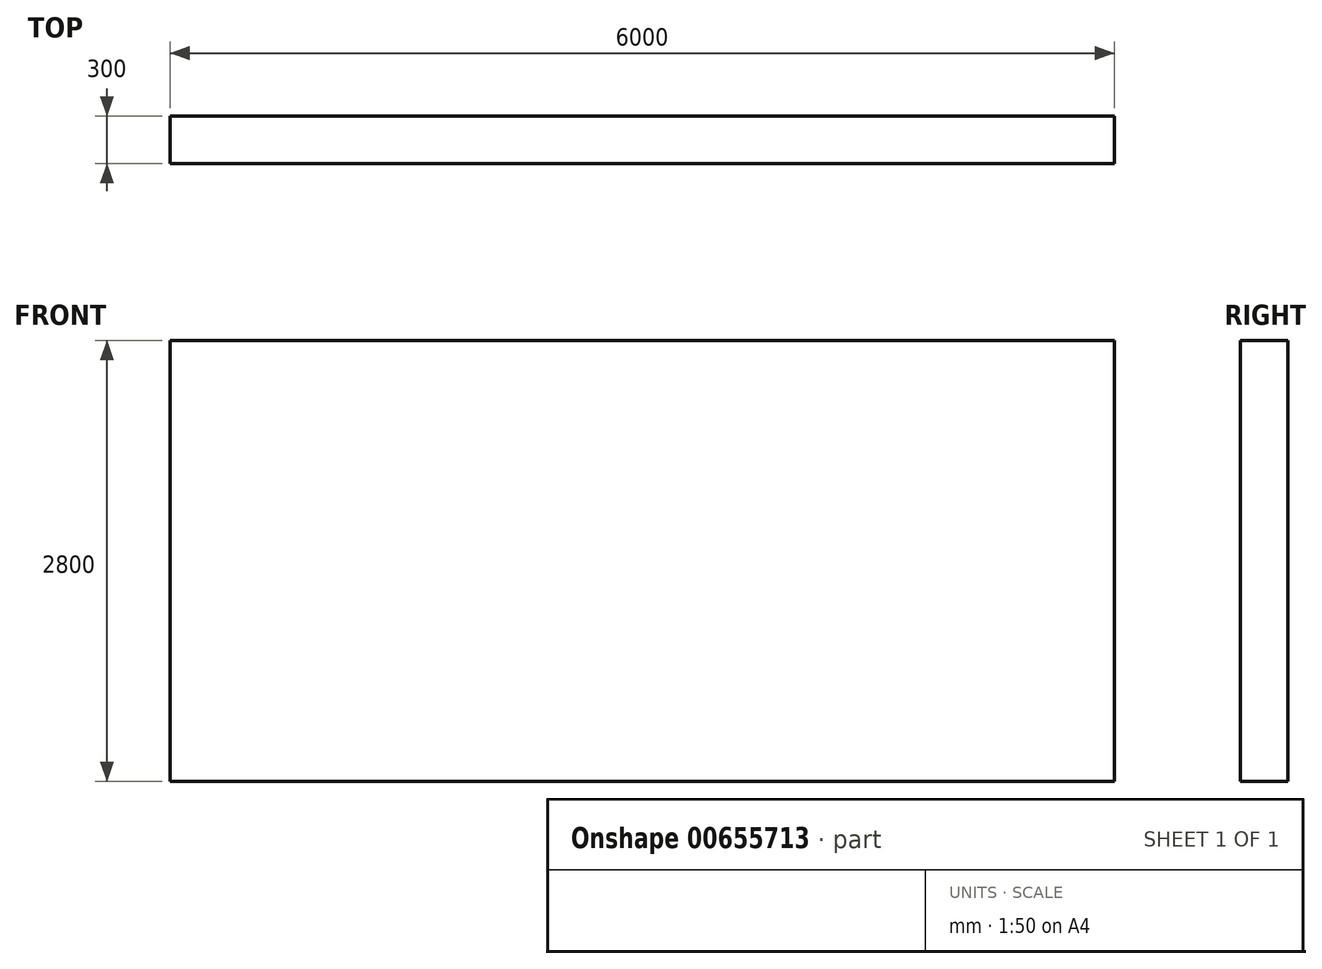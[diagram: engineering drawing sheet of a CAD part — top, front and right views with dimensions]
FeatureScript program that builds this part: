
annotation { "Feature Type Name" : "Feature", "Feature Type Description" : "" }
export const myFeature = defineFeature(function(context is Context, id is Id, definition is map)
    precondition{}
    {
        {
            var Q0;
            Q0=qCreatedBy(makeId("Front.planeOp"),FACE);
            var sketch = newSketch(context, id + "F0", { "sketchPlane" : qUnion([Q0])});
            skLineSegment(sketch, "E0.bottom", {"start": v(-37.63, 2771.36) * mm, "end": v(5962.37, 2771.36) * mm});
            skLineSegment(sketch, "E0.top", {"start": v(-37.63, -28.64) * mm, "end": v(5962.37, -28.64) * mm});
            skLineSegment(sketch, "E0.left", {"start": v(-37.63, 2771.36) * mm, "end": v(-37.63, -28.64) * mm});
            skLineSegment(sketch, "E0.right", {"start": v(5962.37, 2771.36) * mm, "end": v(5962.37, -28.64) * mm});
            skSolve(sketch);
        }
        {
            var Q0;
            Q0=makeQuery(id+"F0.imprint","IMPRINT",FACE,{"disambiguationData":[TD([[makeQuery(id+"F0.imprint","IMPRINT",EDGE,{"derivedFrom":sQuery(id+"F0.wireOp",EDGE,"E0.bottom")}),-1.0]])]});
            extrude(context, id + "F1", {"entities" : qUnion([Q0]), "oppositeDirection" : true, "depth" : 300 * mm, "offsetDistance" : 25 * mm});
        }
    });
